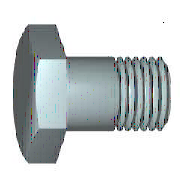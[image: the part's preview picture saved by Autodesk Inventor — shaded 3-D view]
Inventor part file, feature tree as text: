
AUTODESK INVENTOR PART (.ipt)
format: ipt  version: 2020 (Build 240168000, 168)  size: 190,976 bytes
history: native  units: mm (DEFAULTED — no unit token found)
features: sketch x3, other x1, extrude x1, chamfer x1, plane x1
ambient origin geometry x7: Origin, YZ Plane, XZ Plane, X Axis, Y Axis, Z Axis, Center Point
bodies: Solid1 (feature_tree)
feature tree (7):
  other  "轴承体"
  extrude  "头"  Depth=13.0mm
  chamfer  "倒角1"  Distance=3.5mm
  plane  "Work Plane1"
  sketch  "草图1"  dims[d0=14.0mm d1=13.0mm]
  sketch  "草图2"  dims[d2=6.0mm]
  sketch  "草图4"  dims[d12=90.0deg d3=3.5mm d4=0.0mm d5=30.0deg d21=90.0deg d6=0.61345mm d7=0.61355mm d8=0.0mm d9=0.5001mm d10=8.9mm d11=10.0mm d13=0.61355mm d14=6.0mm d15=13.0mm d16=0.0mm d19=10.0mm d55=45.0deg d57=0.0mm d58=0.0mm]
